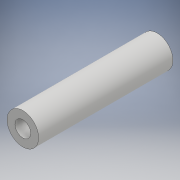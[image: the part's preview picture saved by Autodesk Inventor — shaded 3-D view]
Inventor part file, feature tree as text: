
AUTODESK INVENTOR PART (.ipt)
format: ipt  version: 2018 (Build 220112000, 112)  size: 95,744 bytes
history: native  units: mm
features: extrude x1, sketch x1
ambient origin geometry x8: Origin, YZ Plane, XZ Plane, XY Plane, X Axis, Y Axis, Z Axis, Center Point
bodies: Solid1 (feature_tree)
feature tree (2):
  extrude  "Extrusion1"  Depth=4.0mm
  sketch  "Sketch1"  dims[d0=8.0mm d1=4.0mm d2=34.0mm d3=0.0mm]
